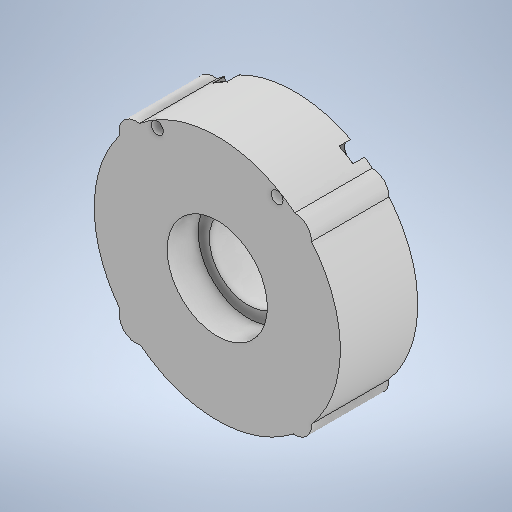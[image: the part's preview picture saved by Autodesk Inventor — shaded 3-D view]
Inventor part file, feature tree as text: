
AUTODESK INVENTOR PART (.ipt)
format: ipt  version: 2025.1 (Build 291241000, 241)  size: 306,176 bytes
history: native  units: mm
features: sketch x6, extrude x5
ambient origin geometry x8: Origin, YZ Plane, XZ Plane, XY Plane, X Axis, Y Axis, Z Axis, Center Point
bodies: Solid1 (feature_tree)
feature tree (11):
  extrude  "Extrusion1"  Depth=10.0mm
  extrude  "Extrusion4"  Depth=70.05mm
  extrude  "Extrusion5"  Depth=74.060786mm
  extrude  "Extrusion6"  Depth=21.9mm TaperAngle=0.0deg
  extrude  "Extrusion8"  Depth=10.0mm TaperAngle=0.0deg
  sketch  "Sketch1"  dims[d0=10.0mm d1=0.25mm]
  sketch  "Skizze - Runde Anordnung1"  dims[d2=40.0mm d4=360.0deg d6=70.05mm]
  sketch  "Skizze4"  dims[d7=0.25mm d8=74.060786mm]
  sketch  "Skizze5"  dims[d9=73.5mm d10=21.9mm d11=0.0mm]
  sketch  "Skizze6"  dims[d24=22.0mm d25=10.0mm d26=0.0mm]
  sketch  "Skizze8"  dims[d27=28.34mm d28=8.76mm d29=0.0mm d30=16.92mm d31=28.34mm d32=3.4mm d33=8.76mm d34=0.0mm d39=5.71mm d40=5.71mm d41=3.29mm d42=0.0mm]
